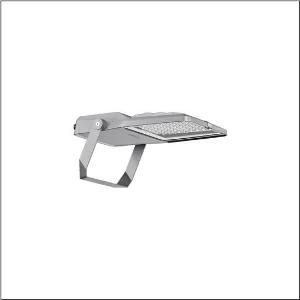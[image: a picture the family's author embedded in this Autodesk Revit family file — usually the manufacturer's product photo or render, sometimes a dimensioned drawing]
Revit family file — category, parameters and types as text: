
# Revit family: floodlight_fl_21_iq_mini___pl61_5xa7772d2c1a_0e67
name_source: partatom
category: Lighting Fixtures
units: mm (PartAtom-declared; Revit-internal decimal feet)

## family parameters
Cut with Voids When Loaded = No
Host = Face
Light Source = No
Part Type = Normal
Room Calculation Point = No
Round Connector Dimension = Use Diameter
Shared = No

## types (1)
- --- (1 x LED, 17500 lm, 143 W, 3000K)
    Apparent Load = 143 VA
    CIE Flux Codes = 33 65 98 100 100
    Color Rendering = 70
    Color Temperature = 3000K
    Default Elevation = 1800 mm
    Description = Floodlight FL 21 iQ mini, floodlight, primary light control with lens, of PMMA, primary optical cover: protective disc, of toughened safety glass, transparent, light distribution: PL61, light emission: direct distribution, installation type: surface-mounted, LED, High Power LED, rated luminous flux: 17.500lm, luminous efficacy: 122lm/W, light colour: 730, colour temperature: 3000K, control: Street-Remote, Auto-Match, Temp-Guard, Night-Set, Smart-Wire, Desk-Remote (wireless, voltage-free reading and setting of iQ features in the workshop via application-optimized NFC function/RFID function), optimised constant luminous flux control (CLO 2.0), with terminal, 6-pole, mains connection: 220..240V, AC, 50/60Hz, start of lifetime: 143W, end of service life: 152W, reduction: 61W, luminaire housing, of diecast aluminium, powder-coated, Siteco® metallic grey (DB 702S), corrosivity category C5 mid according to DIN EN ISO 12944, sealing non-destructively replaceable, mounting bracket, of steel, galvanised, powder-coated, Siteco® metallic grey (DB 702S), protection rating (complete): IP66, insulation class (complete): insulation class II (safety insulation), certification: CE, ENEC, VDE, protection symbol: D, impact resistance: IK08, permissible operating ambient temperature: -40..+40°C, permissible operating ambient temperature for outdoor applications: -40..+50°C, standard: DIN EN 12944, LABS conformity tested according to VDMA 24364:2018-05, packaging unit: 1 piece

Light Distribution: PL61
    Height = 70 mm
    Lamp = 1 x LED
    Lamp Light Flux = 17500 lm
    Lamp Power = 143 W
    Lamp count = 1
    Length = 485 mm
    Luminous efficacy = 122 lm/W
    Manufacturer = Siteco
    ModVariant = No
    Model = 5XA7772D2C1A
    Number of Poles = 1
    OnlyDefault = Yes
    Power Factor = 1
    Product Name = Floodlight FL 21 iQ mini | PL61
    Product group = floodlight | pylon annexe
    ProductGroupID = 6200
    Protection Class = Protection class II
    Protection Degree = IP 66
    RLX_Detail_Level = 1
    RLX_Emergency_Light_Flux = 0 lm
    RLX_Emergency_Type = 0
    RLX_Emergency_Type_DB = No
    RlxData = <blob elided: 96513 chars, md5=a5aed5bb>
    Socket = socket
    Standby Power = 0 W
    System Light Flux = 17500 lm
    System Power = 143 W
    Type Comments = factory setting: luminous flux: 100 % | dim-lin: 254 | 730 mA
    Type Image = l_1006845.jpg
    URL = http://relux.com
    VarID = @adj_123455
    Voltage = 0 V
    Weight = 0.00 kg
    Width = 337 mm

## geometry (parser evidence)
native form markers: Blend x4, Sweep x11
no freeform markers — native parametric forms only
